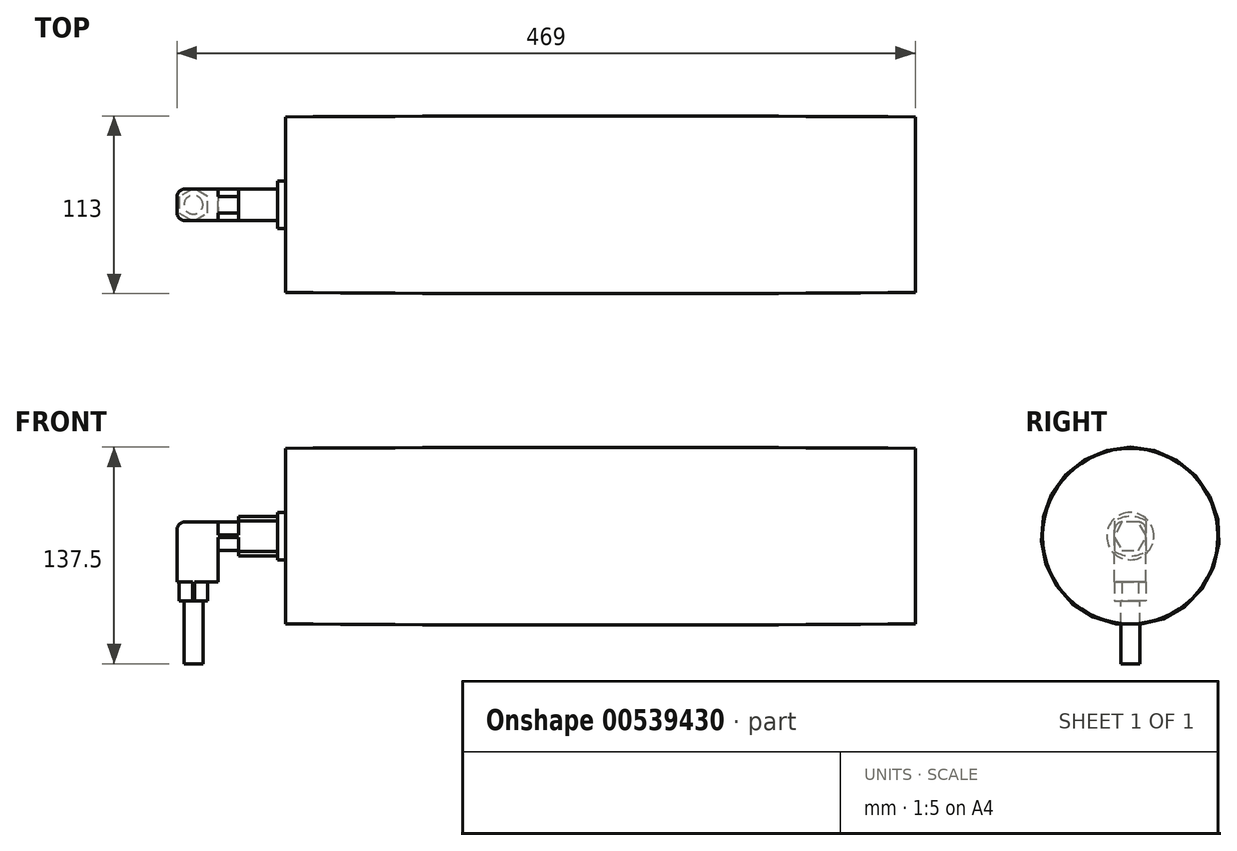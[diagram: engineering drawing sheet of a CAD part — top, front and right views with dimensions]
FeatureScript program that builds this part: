
annotation { "Feature Type Name" : "Feature", "Feature Type Description" : "" }
export const myFeature = defineFeature(function(context is Context, id is Id, definition is map)
    precondition{}
    {
        {
            var Q0;
            Q0=qCreatedBy(makeId("Front.planeOp"),FACE);
            var sketch = newSketch(context, id + "F0", { "sketchPlane" : qUnion([Q0])});
            skLineSegment(sketch, "E0.bottom", {"start": v(-200, 55.75) * mm, "end": v(200, 55.75) * mm});
            skLineSegment(sketch, "E0.top", {"start": v(-200, 0) * mm, "end": v(200, 0) * mm});
            skLineSegment(sketch, "E0.left", {"start": v(-200, 55.75) * mm, "end": v(-200, 0) * mm});
            skLineSegment(sketch, "E0.right", {"start": v(200, 55.75) * mm, "end": v(200, 0) * mm});
            skPoint(sketch, "E0.middle", {"position": v(0, 27.88) * mm});
            skArc(sketch, "E1", {"start": v(200, 55.75) * mm, "mid": v(0, 56.5) * mm, "end": v(-200, 55.75) * mm});
            skSolve(sketch);
        }
        {
            var Q0;
            Q0=makeQuery(id+"F0.imprint","IMPRINT",FACE,{"disambiguationData":[TD([[makeQuery(id+"F0.imprint","IMPRINT",EDGE,{"derivedFrom":sQuery(id+"F0.wireOp",EDGE,"E0.bottom")}),-1.0]])]});
            var Q1;
            Q1=makeQuery(id+"F0.imprint","IMPRINT",FACE,{"disambiguationData":[TD([[makeQuery(id+"F0.imprint","IMPRINT",EDGE,{"derivedFrom":sQuery(id+"F0.wireOp",EDGE,"E0.bottom")}),1.0]])]});
            var Q2;
            Q2=sQuery(id+"F0.wireOp",EDGE,"E0.top");
            revolve(context, id + "F1", {"entities" : qUnion([Q0, Q1]), "axis" : qUnion([Q2]), "revolveType" : RevolveType.FULL});
        }
        {
            var Q0;
            Q0=makeQuery(id+"F1.opRevolve","SWEPT_FACE",FACE,{"disambiguationData":[OSD([sQuery(id+"F0.wireOp",EDGE,"E0.left")])]});
            var sketch = newSketch(context, id + "F2", { "sketchPlane" : qUnion([Q0])});
            skLineSegment(sketch, "E2.bottom", {"start": v(10, 9.67) * mm, "end": v(-10, 9.67) * mm});
            skLineSegment(sketch, "E2.top", {"start": v(10, -9.67) * mm, "end": v(-10, -9.67) * mm});
            skLineSegment(sketch, "E2.left", {"start": v(10, 9.67) * mm, "end": v(10, -9.67) * mm});
            skLineSegment(sketch, "E2.right", {"start": v(-10, 9.67) * mm, "end": v(-10, -9.67) * mm});
            skPoint(sketch, "E2.middle", {"position": v(0, 0) * mm});
            skArc(sketch, "E3", {"start": v(10, 9.67) * mm, "mid": v(0, 12.5) * mm, "end": v(-10, 9.67) * mm});
            skArc(sketch, "E4", {"start": v(-10, -9.67) * mm, "mid": v(0, -12.5) * mm, "end": v(10, -9.67) * mm});
            skSolve(sketch);
        }
        {
            var Q0;
            Q0=makeQuery(id+"F2.imprint","IMPRINT",FACE,{"disambiguationData":[TD([[makeQuery(id+"F2.imprint","IMPRINT",EDGE,{"derivedFrom":sQuery(id+"F2.wireOp",EDGE,"E2.bottom")}),1.0]])]});
            var Q1;
            Q1=makeQuery(id+"F2.imprint","IMPRINT",FACE,{"disambiguationData":[TD([[makeQuery(id+"F2.imprint","IMPRINT",EDGE,{"derivedFrom":sQuery(id+"F2.wireOp",EDGE,"E2.top")}),1.0]])]});
            var Q2;
            Q2=makeQuery(id+"F2.imprint","IMPRINT",FACE,{"disambiguationData":[TD([[makeQuery(id+"F2.imprint","IMPRINT",EDGE,{"derivedFrom":sQuery(id+"F2.wireOp",EDGE,"E2.bottom")}),-1.0]])]});
            extrude(context, id + "F3", {"entities" : qUnion([Q0, Q1, Q2]), "operationType" : NewBodyOperationType.ADD, "depth" : (5 + 25) * mm, "offsetDistance" : 25 * mm});
        }
        {
            var Q0;
            Q0=makeQuery(id+"F1.opRevolve","SWEPT_FACE",FACE,{"disambiguationData":[OSD([sQuery(id+"F0.wireOp",EDGE,"E0.left")])]});
            var sketch = newSketch(context, id + "F4", { "sketchPlane" : qUnion([Q0])});
            skCircle(sketch, "E5", {"center": v(0, 0) * mm, "radius": 15 * mm});
            skSolve(sketch);
        }
        {
            var Q0;
            Q0=makeQuery(id+"F4.imprint","IMPRINT",FACE,{"disambiguationData":[TD([[makeQuery(id+"F4.imprint","IMPRINT",EDGE,{"derivedFrom":sQuery(id+"F4.wireOp",EDGE,"E5")}),1.0]])]});
            extrude(context, id + "F5", {"entities" : qUnion([Q0]), "operationType" : NewBodyOperationType.ADD, "depth" : 5 * mm, "offsetDistance" : 25 * mm});
        }
        {
            var Q0;
            Q0=makeQuery(id+"F3.opExtrude","CAP_FACE",FACE,{"disambiguationData":[OSD([sQuery(id+"F2.wireOp",EDGE,"E2.left"),sQuery(id+"F2.wireOp",EDGE,"E2.right"),sQuery(id+"F2.wireOp",EDGE,"E3"),sQuery(id+"F2.wireOp",EDGE,"E4")])],"isStart":false});
            var sketch = newSketch(context, id + "F6", { "sketchPlane" : qUnion([Q0])});
            skCircle(sketch, "E6.cCircle", {"center": v(0, 0) * mm, "radius": 10.4 * mm, "construction": true});
            skLineSegment(sketch, "E6.0", {"start": v(5.2, 9) * mm, "end": v(10.4, 0) * mm});
            skLineSegment(sketch, "E6.1", {"start": v(10.4, 0) * mm, "end": v(5.2, -9) * mm});
            skLineSegment(sketch, "E6.2", {"start": v(5.2, -9) * mm, "end": v(-5.2, -9) * mm});
            skLineSegment(sketch, "E6.3", {"start": v(-5.2, -9) * mm, "end": v(-10.4, 0) * mm});
            skLineSegment(sketch, "E6.4", {"start": v(-10.4, 0) * mm, "end": v(-5.2, 9) * mm});
            skLineSegment(sketch, "E6.5", {"start": v(-5.2, 9) * mm, "end": v(5.2, 9) * mm});
            skSolve(sketch);
        }
        {
            var Q0;
            {var subQ0=sQuery(id+"F6.wireOp",EDGE,"E6.2");Q0=makeQuery(id+"F6.imprint","IMPRINT",FACE,{"disambiguationData":[TD([[makeQuery(id+"F6.imprint","IMPRINT",EDGE,{"derivedFrom":subQ0}),-1.0]])]});}
            extrude(context, id + "F7", {"entities" : qUnion([Q0]), "operationType" : NewBodyOperationType.ADD, "depth" : 13 * mm, "offsetDistance" : 25 * mm});
        }
        {
            var Q0;
            Q0=makeQuery(id+"F7.opExtrude","SWEPT_FACE",FACE,{"disambiguationData":[OSD([sQuery(id+"F6.wireOp",EDGE,"E6.5")])]});
            var sketch = newSketch(context, id + "F8", { "sketchPlane" : qUnion([Q0])});
            skLineSegment(sketch, "E7.bottom", {"start": v(-269, 10) * mm, "end": v(-243, 10) * mm});
            skLineSegment(sketch, "E7.top", {"start": v(-269, -10) * mm, "end": v(-243, -10) * mm});
            skLineSegment(sketch, "E7.left", {"start": v(-269, 10) * mm, "end": v(-269, -10) * mm});
            skLineSegment(sketch, "E7.right", {"start": v(-243, 10) * mm, "end": v(-243, -10) * mm});
            skPoint(sketch, "E7.middle", {"position": v(-256, 0) * mm});
            skPoint(sketch, "E8.0", {"position": v(-243, 10) * mm});
            skSolve(sketch);
        }
        {
            var Q0;
            {var subQ3=sQuery(id+"F8.wireOp",EDGE,"E7.bottom");Q0=makeQuery(id+"F8.imprint","IMPRINT",FACE,{"disambiguationData":[TD([[makeQuery(id+"F8.imprint","IMPRINT",EDGE,{"derivedFrom":subQ3}),-1.0]])]});}
            extrude(context, id + "F9", {"entities" : qUnion([Q0]), "operationType" : NewBodyOperationType.ADD, "oppositeDirection" : true, "depth" : 50 * mm, "offsetDistance" : 25 * mm});
        }
        {
            var Q0;
            Q0=makeQuery(id+"F9.opExtrude","CAP_FACE",FACE,{"disambiguationData":[OSD([sQuery(id+"F8.wireOp",EDGE,"E7.bottom"),sQuery(id+"F8.wireOp",EDGE,"E7.top"),sQuery(id+"F8.wireOp",EDGE,"E7.left"),sQuery(id+"F8.wireOp",EDGE,"E7.right")])],"isStart":false});
            var sketch = newSketch(context, id + "F10", { "sketchPlane" : qUnion([Q0])});
            skLineSegment(sketch, "E9.0.0", {"start": v(-243, -10) * mm, "end": v(-243, 10) * mm});
            skLineSegment(sketch, "E9.0.1", {"start": v(-243, 10) * mm, "end": v(-269, 10) * mm});
            skLineSegment(sketch, "E9.0.2", {"start": v(-269, 10) * mm, "end": v(-269, -10) * mm});
            skLineSegment(sketch, "E9.0.3", {"start": v(-269, -10) * mm, "end": v(-243, -10) * mm});
            skCircle(sketch, "E10.cCircle", {"center": v(-258.5, 0) * mm, "radius": 10.4 * mm, "construction": true});
            skLineSegment(sketch, "E10.0", {"start": v(-258.5, 10.4) * mm, "end": v(-249.5, 5.2) * mm});
            skLineSegment(sketch, "E10.1", {"start": v(-249.5, 5.2) * mm, "end": v(-249.5, -5.2) * mm});
            skLineSegment(sketch, "E10.2", {"start": v(-249.5, -5.2) * mm, "end": v(-258.5, -10.4) * mm});
            skLineSegment(sketch, "E10.3", {"start": v(-258.5, -10.4) * mm, "end": v(-267.5, -5.2) * mm});
            skLineSegment(sketch, "E10.4", {"start": v(-267.5, -5.2) * mm, "end": v(-267.5, 5.2) * mm});
            skLineSegment(sketch, "E10.5", {"start": v(-267.5, 5.2) * mm, "end": v(-258.5, 10.4) * mm});
            skLineSegment(sketch, "E11.0", {"start": v(-230, -10) * mm, "end": v(-230, 10) * mm});
            skSolve(sketch);
        }
        {
            var Q0;
            {var subQ1=sQuery(id+"F10.wireOp",EDGE,"E9.0.2");Q0=makeQuery(id+"F10.imprint","IMPRINT",FACE,{"disambiguationData":[TD([[makeQuery(id+"F10.imprint","IMPRINT",EDGE,{"derivedFrom":subQ1}),-1.0]])]});}
            var Q1;
            {var subQ5=sQuery(id+"F10.wireOp",EDGE,"E9.0.0");Q1=makeQuery(id+"F10.imprint","IMPRINT",FACE,{"disambiguationData":[TD([[makeQuery(id+"F10.imprint","IMPRINT",EDGE,{"derivedFrom":subQ5}),1.0]])]});}
            extrude(context, id + "F11", {"entities" : qUnion([Q0, Q1]), "operationType" : NewBodyOperationType.REMOVE, "oppositeDirection" : true, "depth" : 12 * mm, "offsetDistance" : 25 * mm});
        }
        {
            var Q0;
            Q0=makeQuery(id+"F9.opExtrude","CAP_FACE",FACE,{"disambiguationData":[OSD([sQuery(id+"F8.wireOp",EDGE,"E7.bottom"),sQuery(id+"F8.wireOp",EDGE,"E7.top"),sQuery(id+"F8.wireOp",EDGE,"E7.left"),sQuery(id+"F8.wireOp",EDGE,"E7.right")])],"isStart":false});
            var sketch = newSketch(context, id + "F12", { "sketchPlane" : qUnion([Q0])});
            skCircle(sketch, "E12", {"center": v(-258.5, 0) * mm, "radius": 6 * mm});
            skLineSegment(sketch, "E13.0", {"start": v(-230, -10) * mm, "end": v(-230, 10) * mm});
            skSolve(sketch);
        }
        {
            var Q0;
            Q0=makeQuery(id+"F12.imprint","IMPRINT",FACE,{"disambiguationData":[TD([[makeQuery(id+"F12.imprint","IMPRINT",EDGE,{"derivedFrom":sQuery(id+"F12.wireOp",EDGE,"E12")}),1.0]])]});
            extrude(context, id + "F13", {"entities" : qUnion([Q0]), "operationType" : NewBodyOperationType.ADD, "depth" : 40 * mm, "offsetDistance" : 25 * mm});
        }
        {
            var Q0;
            Q0=makeQuery(id+"F9.opExtrude","SWEPT_EDGE",EDGE,{"disambiguationData":[OSD([sQuery(id+"F8.wireOp",EDGE,"E7.top"),sQuery(id+"F8.wireOp",EDGE,"E7.left")])]});
            var Q1;
            Q1=makeQuery(id+"F9.opExtrude","SWEPT_EDGE",EDGE,{"disambiguationData":[OSD([sQuery(id+"F8.wireOp",EDGE,"E7.bottom"),sQuery(id+"F8.wireOp",EDGE,"E7.left")])]});
            var Q2;
            Q2=makeQuery(id+"F9.opExtrude","CAP_EDGE",EDGE,{"disambiguationData":[OSD([sQuery(id+"F8.wireOp",EDGE,"E7.left")])],"isStart":true});
            var Q3;
            Q3=makeQuery(id+"F9.opExtrude","CAP_EDGE",EDGE,{"disambiguationData":[OSD([sQuery(id+"F8.wireOp",EDGE,"E7.top")])],"isStart":true});
            var Q4;
            Q4=makeQuery(id+"F9.opExtrude","CAP_EDGE",EDGE,{"disambiguationData":[OSD([sQuery(id+"F8.wireOp",EDGE,"E7.bottom")])],"isStart":true});
            fillet(context, id + "F14", {"entities" : qUnion([Q0, Q1, Q2, Q3, Q4]), "radius" : 5 * mm, "tangentPropagation" : true, "allowEdgeOverflow" : false});
        }
    });
